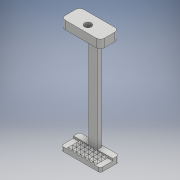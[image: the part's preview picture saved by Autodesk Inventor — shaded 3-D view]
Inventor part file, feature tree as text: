
AUTODESK INVENTOR PART (.ipt)
format: ipt  version: 2017 (Build 210142000, 142)  size: 257,536 bytes
history: native  units: mm
features: extrude x9, sketch x8, fillet x2, chamfer x2, projected_geometry x2
ambient origin geometry x8: Origin, YZ Plane, XZ Plane, XY Plane, X Axis, Y Axis, Z Axis, Center Point
bodies: Solid1 (feature_tree)
feature tree (23):
  extrude  "Extrusion1"  Depth=9.0mm
  extrude  "Extrusion2"  Depth=2.0mm
  sketch  "Sketch6"  dims[d5=2.0mm d6=1.5mm d7=0.0mm]
  extrude  "Extrusion5"  Depth=2.0mm TaperAngle=0.0deg
  extrude  "Extrusion6"  Depth=4.0mm TaperAngle=0.0deg
  extrude  "Extrusion7"  Depth=4.0mm
  extrude  "Extrusion8"  Depth=1.0mm
  extrude  "Extrusion9"  TaperAngle=135.0deg  [1 undecoded]
  fillet  "Fillet2"  [1 undecoded]
  fillet  "Fillet3"  Radius=4.0mm
  extrude  "Extrusion10"  Depth=2.0mm
  extrude  "Extrusion11"  Depth=2.0mm
  chamfer  "Chamfer3"  Distance=6.0mm
  chamfer  "Chamfer4"  Distance=1.0mm
  sketch  "Sketch1"  dims[d0=19.0mm d1=9.0mm]
  sketch  "Sketch2"  dims[d2=3.0mm d3=0.0mm d4=2.0mm]
  sketch  "Sketch7"  dims[d13=4.0mm d14=47.0mm d15=0.0mm]
  projected_geometry  "Projected Loop2"
  sketch  "Sketch8"  dims[d16=4.0mm d17=0.0mm d18=3.3mm]
  projected_geometry  "Projected Loop3"
  sketch  "Sketch10"  dims[d19=4.0mm d20=0.0mm d23=1.0mm]
  sketch  "Sketch11"  dims[d24=6.0mm d25=135.0deg d26=90.0deg d27=4.0mm d28=0.0mm]
  sketch  "Sketch12"  dims[d30=135.0deg d31=40.0mm d33=2.0mm d34=10.0mm d36=10.0mm d38=40.0mm d40=2.0mm d41=10.0mm d43=10.0mm d45=6.0mm d46=0.0mm d47=1.0mm d48=2.0mm d55=10.0mm d56=0.0mm d57=4.0mm d58=0.0mm d59=2.0mm d60=1.0mm d61=45.0deg d62=2.0mm d63=1.0mm d64=45.0deg d66=5.5mm]
note: 2 required parameter values undecoded (feature->parameter linkage not recoverable at this tier; creation-order binding heuristic only, values carry confidence <= 0.55)
